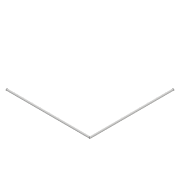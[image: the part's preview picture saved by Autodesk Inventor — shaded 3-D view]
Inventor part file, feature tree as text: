
AUTODESK INVENTOR PART (.ipt)
format: ipt  version: 2017 (Build 210142000, 142)  size: 78,336 bytes
history: native  units: mm
features: sketch x2, sweep x1
ambient origin geometry x8: Origin, YZ Plane, XZ Plane, XY Plane, X Axis, Y Axis, Z Axis, Center Point
bodies: Solid1 (feature_tree)
feature tree (3):
  sweep  "Sweep1"
  sketch  "Sketch1"  dims[d0=500.0mm d1=500.0mm]
  sketch  "Sketch2"  dims[d2=10.0mm d3=0.0mm d4=0.0mm]
